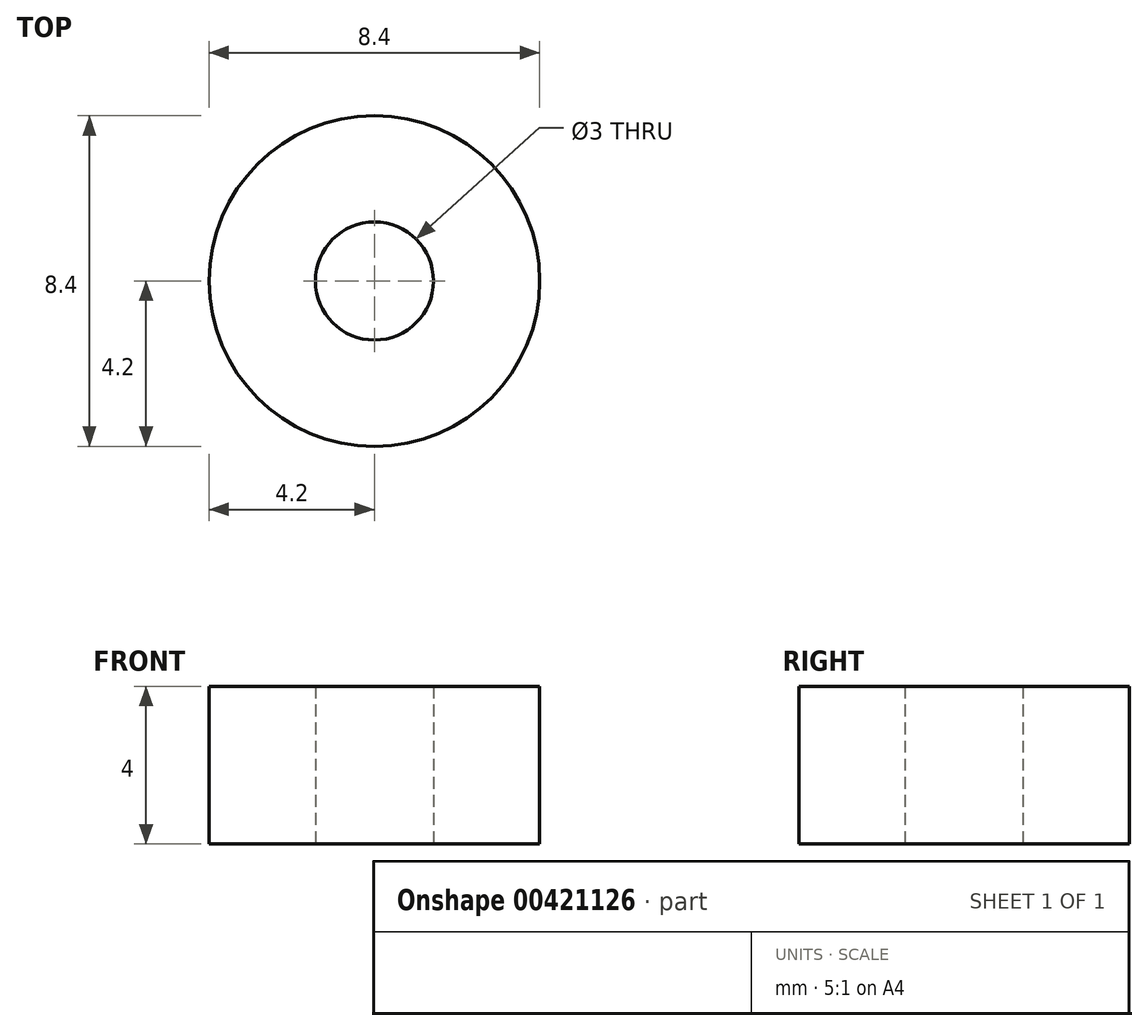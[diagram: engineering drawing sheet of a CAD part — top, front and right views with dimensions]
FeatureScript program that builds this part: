
annotation { "Feature Type Name" : "Feature", "Feature Type Description" : "" }
export const myFeature = defineFeature(function(context is Context, id is Id, definition is map)
    precondition{}
    {
        {
            var Q0;
            Q0=qCreatedBy(makeId("Top.planeOp"),FACE);
            var sketch = newSketch(context, id + "F0", { "sketchPlane" : qUnion([Q0])});
            skCircle(sketch, "E0", {"center": v(0, 0) * mm, "radius": 4.2 * mm});
            skCircle(sketch, "E1", {"center": v(0, 0) * mm, "radius": 1.5 * mm});
            skSolve(sketch);
        }
        {
            var Q0;
            Q0 = qSketchRegion(id + "F0", true);
            extrude(context, id + "F1", {"entities" : qUnion([Q0]), "depth" : 4 * mm});
        }
    });
